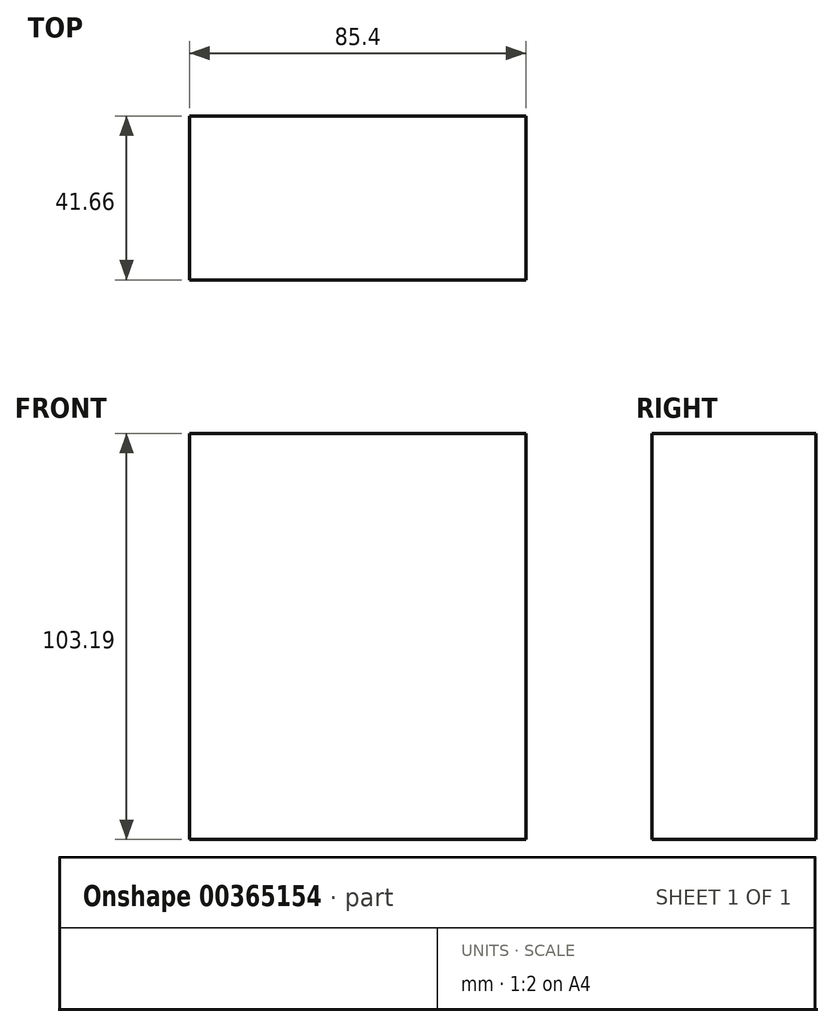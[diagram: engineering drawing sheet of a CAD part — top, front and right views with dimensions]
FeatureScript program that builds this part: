
annotation { "Feature Type Name" : "Feature", "Feature Type Description" : "" }
export const myFeature = defineFeature(function(context is Context, id is Id, definition is map)
    precondition{}
    {
        {
            var Q0;
            Q0=qCreatedBy(makeId("Front.planeOp"),FACE);
            var sketch = newSketch(context, id + "F0", { "sketchPlane" : qUnion([Q0])});
            skLineSegment(sketch, "E0.bottom", {"start": v(-48.65, 68.5) * mm, "end": v(36.75, 68.5) * mm});
            skLineSegment(sketch, "E0.top", {"start": v(-48.65, -34.68) * mm, "end": v(36.75, -34.68) * mm});
            skLineSegment(sketch, "E0.left", {"start": v(-48.65, 68.5) * mm, "end": v(-48.65, -34.68) * mm});
            skLineSegment(sketch, "E0.right", {"start": v(36.75, 68.5) * mm, "end": v(36.75, -34.68) * mm});
            skSolve(sketch);
        }
        {
            var Q0;
            Q0 = qSketchRegion(id + "F0", true);
            extrude(context, id + "F1", {"entities" : qUnion([Q0]), "depth" : 41.66 * mm});
        }
    });
